# Revit family: P300253-031
name_source: partatom
category: Lighting Fixtures
revit_build: Autodesk Revit 2014 (Build: 20130308_1515(x64)
units: mm (PartAtom-declared; Revit-internal decimal feet)

## types (1)
- P300253-031
    Apparent Load = 60 VA
    Assembly Code = D5020200
    Color Filter = 16777215
    Connector Description = Lighting Connector
    Default Elevation = 48"
    Depth = 7"
    Description = Beautiful lighting will appeal to both your classic taste and your artistic spirit with this bath light. Wandering eyes will focus on a clear chiseled glass shade as it offers an air of refinery. A handsome black light base is supported by a dainty curved arm to complete the elegant design.
    Dimming Lamp Color Temperature Shift = <None>
    Fixture distribution = Direct
    Glass = Hubbell - Glass
    Gold = Hubbell - Gold
    Height = 6 1/8"
    Housing Material = Paint - Hubbell - Textured Camera Black
    Lamp = Medium Base or LED
    Load Classification = Lighting
    Manufacturer = Progress Lighting
    Model = P300253-031
    Photometric Web File = generic
    Power Factor = 1
    Product Documentation Link = https://hubbellcdn.com
    Product Link = https://www.hubbell.com
    Specifications = • Wandering eyes will focus on a clear chiseled glass shade as it offers an air of refinery.
• A handsome black light base is supported by a dainty curved arm to complete the elegant
design.
• Beautiful lighting will appeal to both your classic taste and your artistic spirit with this bath
light.
• Ideal for any bathroom.
• Perfect for transitional, rustic, farmhouse, or coastal settings.
• Measures 5-inch width by 10-3/8-inch height.
• Uses one medium base bulb that is sold separately (60w max - LED or incandescent).
• Able to be fully dimmable with dimmable bulbs.
• Includes installation instructions and mounting hardware.
• Progress Lighting products are designed for exceptional quality, reliability, and functionality
    Tilt Angle = 60.00°
    URL = https://www.hubbell.com
    Voltage = 120 V
    Warranty = 5 years Warranty
    Wattage Comments = 60W
    Watts = 60 W
    White = Paint - Hubbell - Matte White
    Width = 10"

## geometry (parser evidence)
native form markers: Sweep x2
no freeform markers — native parametric forms only
